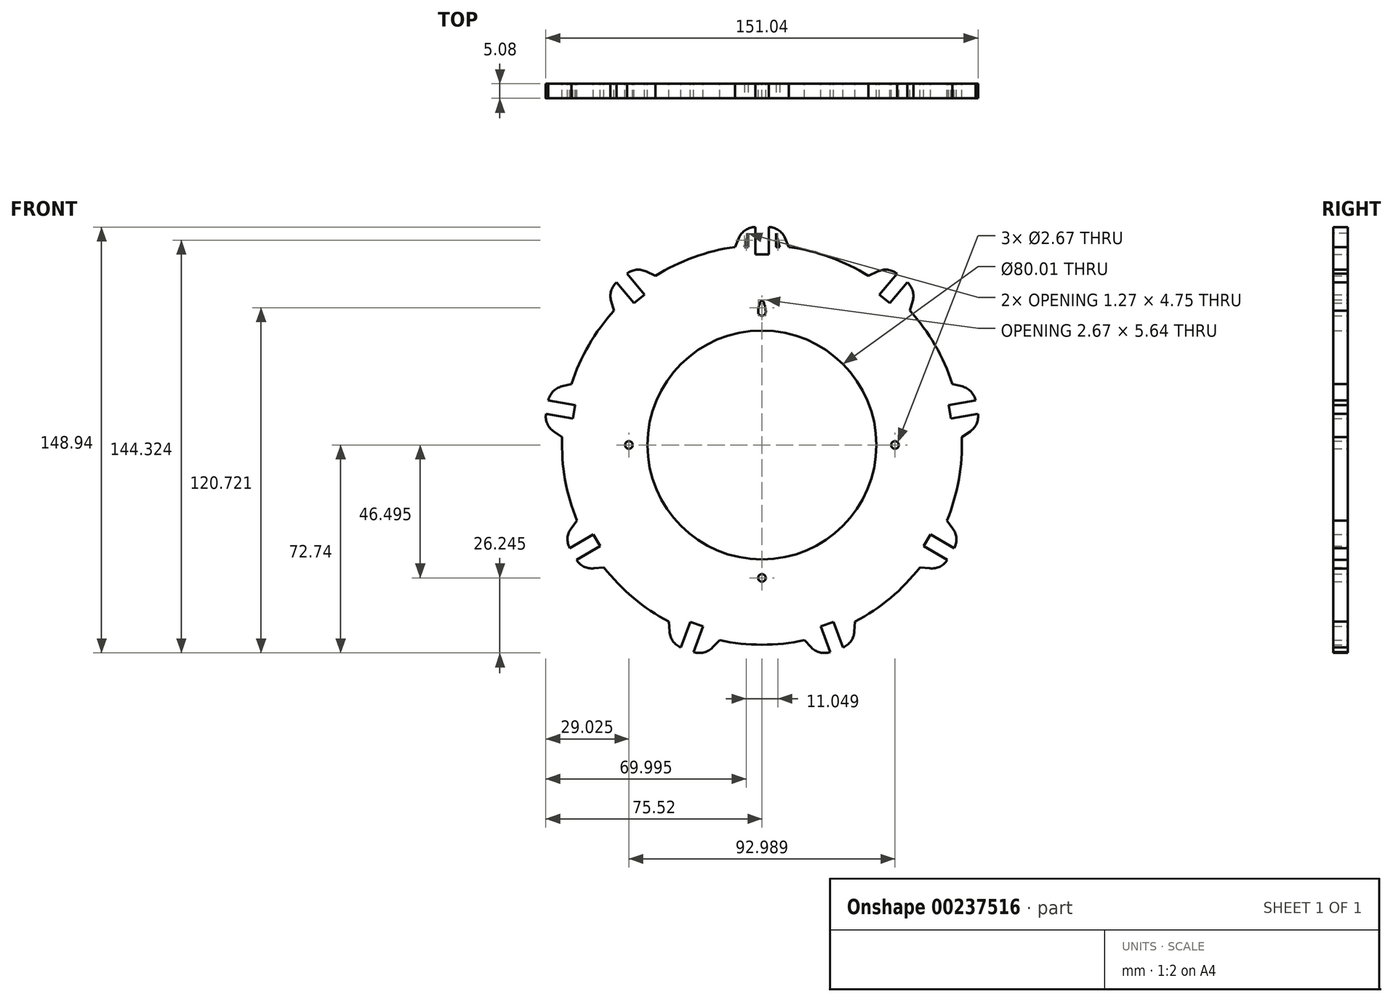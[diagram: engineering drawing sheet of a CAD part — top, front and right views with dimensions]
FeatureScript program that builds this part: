
annotation { "Feature Type Name" : "Feature", "Feature Type Description" : "" }
export const myFeature = defineFeature(function(context is Context, id is Id, definition is map)
    precondition{}
    {
        {
            var Q0;
            Q0=qCreatedBy(makeId("Front.planeOp"),FACE);
            var sketch = newSketch(context, id + "F0", { "sketchPlane" : qUnion([Q0])});
            skCircle(sketch, "E0", {"center": v(0, 0) * mm, "radius": 69.85 * mm});
            skCircle(sketch, "E1", {"center": v(0, 0) * mm, "radius": 40 * mm});
            skCircle(sketch, "E2", {"center": v(0, 0) * mm, "radius": 46.5 * mm, "construction": true});
            skPoint(sketch, "E3.center", {"position": v(0, -7.07) * mm});
            skLineSegment(sketch, "E4", {"start": v(-9.44, 69.2) * mm, "end": v(-8.02, 72.42) * mm});
            skLineSegment(sketch, "E5", {"start": v(-2.21, 76.2) * mm, "end": v(2.21, 76.2) * mm});
            skLineSegment(sketch, "E6", {"start": v(8.02, 72.42) * mm, "end": v(9.44, 69.2) * mm});
            skPoint(sketch, "E7", {"position": v(0, 76.2) * mm});
            skLineSegment(sketch, "E8", {"start": v(-9.44, 69.2) * mm, "end": v(-40, 0) * mm, "construction": true});
            skLineSegment(sketch, "E9", {"start": v(40, 0) * mm, "end": v(9.44, 69.2) * mm, "construction": true});
            skLineSegment(sketch, "E10", {"start": v(-2.35, 76.2) * mm, "end": v(-2.35, 66.67) * mm});
            skLineSegment(sketch, "E11", {"start": v(-2.35, 66.68) * mm, "end": v(2.35, 66.68) * mm});
            skLineSegment(sketch, "E12", {"start": v(2.35, 66.67) * mm, "end": v(2.35, 76.2) * mm});
            skPoint(sketch, "E13", {"position": v(0, 66.67) * mm});
            skPoint(sketch, "E14.visualSharp", {"position": v(-6.35, 76.2) * mm});
            skArc(sketch, "E14.filletArc", {"start": v(-2.21, 76.2) * mm, "mid": v(-5.68, 75.17) * mm, "end": v(-8.02, 72.42) * mm});
            skPoint(sketch, "E15.visualSharp", {"position": v(6.35, 76.2) * mm});
            skArc(sketch, "E15.filletArc", {"start": v(8.02, 72.42) * mm, "mid": v(5.68, 75.17) * mm, "end": v(2.21, 76.2) * mm});
            skCircle(sketch, "E16.MirrorC", {"center": v(0, 46.5) * mm, "radius": 1.33 * mm});
            skCircle(sketch, "E17", {"center": v(0, 0) * mm, "radius": 66.72 * mm, "construction": true});
            skCircle(sketch, "E18.1.0", {"center": v(-46.5, 0) * mm, "radius": 1.33 * mm});
            skCircle(sketch, "E18.2.0", {"center": v(0, -46.5) * mm, "radius": 1.33 * mm});
            skCircle(sketch, "E18.3.0", {"center": v(46.5, 0) * mm, "radius": 1.33 * mm});
            skCircle(sketch, "E19", {"center": v(0, 0) * mm, "radius": 50.8 * mm, "construction": true});
            skArc(sketch, "E20", {"start": v(1.33, 46.48) * mm, "mid": v(1, 48.74) * mm, "end": v(0, 50.8) * mm});
            skArc(sketch, "E21", {"start": v(0, 50.8) * mm, "mid": v(-1, 48.74) * mm, "end": v(-1.33, 46.48) * mm});
            skLineSegment(sketch, "E22.1.0", {"start": v(-51.72, 46.95) * mm, "end": v(-52.7, 50.32) * mm});
            skArc(sketch, "E22.1.1", {"start": v(-50.68, 56.95) * mm, "mid": v(-52.67, 53.93) * mm, "end": v(-52.7, 50.32) * mm});
            skLineSegment(sketch, "E22.1.2", {"start": v(-50.78, 56.86) * mm, "end": v(-44.66, 49.57) * mm});
            skLineSegment(sketch, "E22.1.3", {"start": v(-41.06, 52.59) * mm, "end": v(-47.18, 59.88) * mm});
            skArc(sketch, "E22.1.4", {"start": v(-40.4, 60.63) * mm, "mid": v(-43.97, 61.23) * mm, "end": v(-47.29, 59.8) * mm});
            skLineSegment(sketch, "E22.1.5", {"start": v(-40.4, 60.63) * mm, "end": v(-37.26, 59.08) * mm});
            skLineSegment(sketch, "E22.1.6", {"start": v(-44.66, 49.57) * mm, "end": v(-41.06, 52.59) * mm});
            skLineSegment(sketch, "E22.2.0", {"start": v(-69.8, 2.72) * mm, "end": v(-72.7, 4.68) * mm});
            skArc(sketch, "E22.2.1", {"start": v(-75.43, 11.05) * mm, "mid": v(-75.01, 7.46) * mm, "end": v(-72.7, 4.68) * mm});
            skLineSegment(sketch, "E22.2.2", {"start": v(-75.45, 10.92) * mm, "end": v(-66.07, 9.26) * mm});
            skLineSegment(sketch, "E22.2.3", {"start": v(-65.25, 13.9) * mm, "end": v(-74.63, 15.55) * mm});
            skArc(sketch, "E22.2.4", {"start": v(-69.92, 20.47) * mm, "mid": v(-73.04, 18.65) * mm, "end": v(-74.66, 15.41) * mm});
            skLineSegment(sketch, "E22.2.5", {"start": v(-69.92, 20.47) * mm, "end": v(-66.52, 21.31) * mm});
            skLineSegment(sketch, "E22.2.6", {"start": v(-66.07, 9.26) * mm, "end": v(-65.25, 13.9) * mm});
            skLineSegment(sketch, "E22.3.0", {"start": v(-55.22, -42.78) * mm, "end": v(-58.7, -43.15) * mm});
            skArc(sketch, "E22.3.1", {"start": v(-64.88, -40.02) * mm, "mid": v(-62.26, -42.5) * mm, "end": v(-58.7, -43.15) * mm});
            skLineSegment(sketch, "E22.3.2", {"start": v(-64.82, -40.13) * mm, "end": v(-56.57, -35.37) * mm});
            skLineSegment(sketch, "E22.3.3", {"start": v(-58.92, -31.3) * mm, "end": v(-67.17, -36.07) * mm});
            skArc(sketch, "E22.3.4", {"start": v(-66.72, -29.26) * mm, "mid": v(-67.94, -32.67) * mm, "end": v(-67.1, -36.18) * mm});
            skLineSegment(sketch, "E22.3.5", {"start": v(-66.72, -29.26) * mm, "end": v(-64.66, -26.43) * mm});
            skLineSegment(sketch, "E22.3.6", {"start": v(-56.57, -35.37) * mm, "end": v(-58.92, -31.3) * mm});
            skLineSegment(sketch, "E22.4.0", {"start": v(-14.8, -68.26) * mm, "end": v(-17.23, -70.8) * mm});
            skArc(sketch, "E22.4.1", {"start": v(-23.98, -72.36) * mm, "mid": v(-20.37, -72.58) * mm, "end": v(-17.23, -70.8) * mm});
            skLineSegment(sketch, "E22.4.2", {"start": v(-23.85, -72.4) * mm, "end": v(-20.6, -63.46) * mm});
            skLineSegment(sketch, "E22.4.3", {"start": v(-25.01, -61.85) * mm, "end": v(-28.27, -70.8) * mm});
            skArc(sketch, "E22.4.4", {"start": v(-32.3, -65.3) * mm, "mid": v(-31.05, -68.7) * mm, "end": v(-28.14, -70.85) * mm});
            skLineSegment(sketch, "E22.4.5", {"start": v(-32.3, -65.3) * mm, "end": v(-32.54, -61.8) * mm});
            skLineSegment(sketch, "E22.4.6", {"start": v(-20.6, -63.46) * mm, "end": v(-25.01, -61.85) * mm});
            skLineSegment(sketch, "E22.5.0", {"start": v(32.54, -61.8) * mm, "end": v(32.3, -65.3) * mm});
            skArc(sketch, "E22.5.1", {"start": v(28.14, -70.85) * mm, "mid": v(31.05, -68.7) * mm, "end": v(32.3, -65.3) * mm});
            skLineSegment(sketch, "E22.5.2", {"start": v(28.27, -70.8) * mm, "end": v(25.01, -61.85) * mm});
            skLineSegment(sketch, "E22.5.3", {"start": v(20.6, -63.46) * mm, "end": v(23.85, -72.4) * mm});
            skArc(sketch, "E22.5.4", {"start": v(17.23, -70.8) * mm, "mid": v(20.37, -72.58) * mm, "end": v(23.98, -72.36) * mm});
            skLineSegment(sketch, "E22.5.5", {"start": v(17.23, -70.8) * mm, "end": v(14.8, -68.26) * mm});
            skLineSegment(sketch, "E22.5.6", {"start": v(25.01, -61.85) * mm, "end": v(20.6, -63.46) * mm});
            skLineSegment(sketch, "E22.6.0", {"start": v(64.66, -26.43) * mm, "end": v(66.72, -29.26) * mm});
            skArc(sketch, "E22.6.1", {"start": v(67.1, -36.18) * mm, "mid": v(67.94, -32.67) * mm, "end": v(66.72, -29.26) * mm});
            skLineSegment(sketch, "E22.6.2", {"start": v(67.17, -36.07) * mm, "end": v(58.92, -31.3) * mm});
            skLineSegment(sketch, "E22.6.3", {"start": v(56.57, -35.37) * mm, "end": v(64.82, -40.13) * mm});
            skArc(sketch, "E22.6.4", {"start": v(58.7, -43.15) * mm, "mid": v(62.26, -42.5) * mm, "end": v(64.88, -40.02) * mm});
            skLineSegment(sketch, "E22.6.5", {"start": v(58.7, -43.15) * mm, "end": v(55.22, -42.78) * mm});
            skLineSegment(sketch, "E22.6.6", {"start": v(58.92, -31.3) * mm, "end": v(56.57, -35.37) * mm});
            skLineSegment(sketch, "E22.7.0", {"start": v(66.52, 21.31) * mm, "end": v(69.92, 20.47) * mm});
            skArc(sketch, "E22.7.1", {"start": v(74.66, 15.41) * mm, "mid": v(73.04, 18.65) * mm, "end": v(69.92, 20.47) * mm});
            skLineSegment(sketch, "E22.7.2", {"start": v(74.63, 15.55) * mm, "end": v(65.25, 13.9) * mm});
            skLineSegment(sketch, "E22.7.3", {"start": v(66.07, 9.26) * mm, "end": v(75.45, 10.92) * mm});
            skArc(sketch, "E22.7.4", {"start": v(72.7, 4.68) * mm, "mid": v(75.01, 7.46) * mm, "end": v(75.43, 11.05) * mm});
            skLineSegment(sketch, "E22.7.5", {"start": v(72.7, 4.68) * mm, "end": v(69.8, 2.72) * mm});
            skLineSegment(sketch, "E22.7.6", {"start": v(65.25, 13.9) * mm, "end": v(66.07, 9.26) * mm});
            skLineSegment(sketch, "E22.8.0", {"start": v(37.26, 59.08) * mm, "end": v(40.4, 60.63) * mm});
            skArc(sketch, "E22.8.1", {"start": v(47.29, 59.8) * mm, "mid": v(43.97, 61.23) * mm, "end": v(40.4, 60.63) * mm});
            skLineSegment(sketch, "E22.8.2", {"start": v(47.18, 59.88) * mm, "end": v(41.06, 52.59) * mm});
            skLineSegment(sketch, "E22.8.3", {"start": v(44.66, 49.57) * mm, "end": v(50.78, 56.86) * mm});
            skArc(sketch, "E22.8.4", {"start": v(52.7, 50.32) * mm, "mid": v(52.67, 53.93) * mm, "end": v(50.68, 56.95) * mm});
            skLineSegment(sketch, "E22.8.5", {"start": v(52.7, 50.32) * mm, "end": v(51.72, 46.95) * mm});
            skLineSegment(sketch, "E22.8.6", {"start": v(41.06, 52.59) * mm, "end": v(44.66, 49.57) * mm});
            skSolve(sketch);
        }
        {
            var Q0;
            Q0=makeQuery(id+"F0.imprint","IMPRINT",FACE,{"disambiguationData":[TD([[makeQuery(id+"F0.imprint","IMPRINT",EDGE,{"derivedFrom":sQuery(id+"F0.wireOp",EDGE,"E1")}),-1.0]])]});
            var Q1;
            {var subQ0=sQuery(id+"F0.wireOp",EDGE,"E22.1.5");Q1=makeQuery(id+"F0.imprint","IMPRINT",FACE,{"disambiguationData":[TD([[makeQuery(id+"F0.imprint","IMPRINT",EDGE,{"derivedFrom":subQ0}),-1.0]])]});}
            var Q2;
            {var subQ0=sQuery(id+"F0.wireOp",EDGE,"E22.1.0");Q2=makeQuery(id+"F0.imprint","IMPRINT",FACE,{"disambiguationData":[TD([[makeQuery(id+"F0.imprint","IMPRINT",EDGE,{"derivedFrom":subQ0}),-1.0]])]});}
            var Q3;
            {var subQ0=sQuery(id+"F0.wireOp",EDGE,"E4");Q3=makeQuery(id+"F0.imprint","IMPRINT",FACE,{"disambiguationData":[TD([[makeQuery(id+"F0.imprint","IMPRINT",EDGE,{"derivedFrom":subQ0}),-1.0]])]});}
            var Q4;
            {var subQ0=sQuery(id+"F0.wireOp",EDGE,"E6");Q4=makeQuery(id+"F0.imprint","IMPRINT",FACE,{"disambiguationData":[TD([[makeQuery(id+"F0.imprint","IMPRINT",EDGE,{"derivedFrom":subQ0}),-1.0]])]});}
            var Q5;
            {var subQ0=sQuery(id+"F0.wireOp",EDGE,"E22.8.0");Q5=makeQuery(id+"F0.imprint","IMPRINT",FACE,{"disambiguationData":[TD([[makeQuery(id+"F0.imprint","IMPRINT",EDGE,{"derivedFrom":subQ0}),-1.0]])]});}
            var Q6;
            {var subQ0=sQuery(id+"F0.wireOp",EDGE,"E22.8.5");Q6=makeQuery(id+"F0.imprint","IMPRINT",FACE,{"disambiguationData":[TD([[makeQuery(id+"F0.imprint","IMPRINT",EDGE,{"derivedFrom":subQ0}),-1.0]])]});}
            var Q7;
            {var subQ0=sQuery(id+"F0.wireOp",EDGE,"E22.7.0");Q7=makeQuery(id+"F0.imprint","IMPRINT",FACE,{"disambiguationData":[TD([[makeQuery(id+"F0.imprint","IMPRINT",EDGE,{"derivedFrom":subQ0}),-1.0]])]});}
            var Q8;
            {var subQ0=sQuery(id+"F0.wireOp",EDGE,"E22.7.5");Q8=makeQuery(id+"F0.imprint","IMPRINT",FACE,{"disambiguationData":[TD([[makeQuery(id+"F0.imprint","IMPRINT",EDGE,{"derivedFrom":subQ0}),-1.0]])]});}
            var Q9;
            {var subQ0=sQuery(id+"F0.wireOp",EDGE,"E22.6.0");Q9=makeQuery(id+"F0.imprint","IMPRINT",FACE,{"disambiguationData":[TD([[makeQuery(id+"F0.imprint","IMPRINT",EDGE,{"derivedFrom":subQ0}),-1.0]])]});}
            var Q10;
            {var subQ0=sQuery(id+"F0.wireOp",EDGE,"E22.6.5");Q10=makeQuery(id+"F0.imprint","IMPRINT",FACE,{"disambiguationData":[TD([[makeQuery(id+"F0.imprint","IMPRINT",EDGE,{"derivedFrom":subQ0}),-1.0]])]});}
            var Q11;
            {var subQ0=sQuery(id+"F0.wireOp",EDGE,"E22.5.5");Q11=makeQuery(id+"F0.imprint","IMPRINT",FACE,{"disambiguationData":[TD([[makeQuery(id+"F0.imprint","IMPRINT",EDGE,{"derivedFrom":subQ0}),-1.0]])]});}
            var Q12;
            {var subQ0=sQuery(id+"F0.wireOp",EDGE,"E22.5.0");Q12=makeQuery(id+"F0.imprint","IMPRINT",FACE,{"disambiguationData":[TD([[makeQuery(id+"F0.imprint","IMPRINT",EDGE,{"derivedFrom":subQ0}),-1.0]])]});}
            var Q13;
            {var subQ0=sQuery(id+"F0.wireOp",EDGE,"E22.4.5");Q13=makeQuery(id+"F0.imprint","IMPRINT",FACE,{"disambiguationData":[TD([[makeQuery(id+"F0.imprint","IMPRINT",EDGE,{"derivedFrom":subQ0}),-1.0]])]});}
            var Q14;
            {var subQ0=sQuery(id+"F0.wireOp",EDGE,"E22.4.0");Q14=makeQuery(id+"F0.imprint","IMPRINT",FACE,{"disambiguationData":[TD([[makeQuery(id+"F0.imprint","IMPRINT",EDGE,{"derivedFrom":subQ0}),-1.0]])]});}
            var Q15;
            {var subQ0=sQuery(id+"F0.wireOp",EDGE,"E22.3.0");Q15=makeQuery(id+"F0.imprint","IMPRINT",FACE,{"disambiguationData":[TD([[makeQuery(id+"F0.imprint","IMPRINT",EDGE,{"derivedFrom":subQ0}),-1.0]])]});}
            var Q16;
            {var subQ0=sQuery(id+"F0.wireOp",EDGE,"E22.3.5");Q16=makeQuery(id+"F0.imprint","IMPRINT",FACE,{"disambiguationData":[TD([[makeQuery(id+"F0.imprint","IMPRINT",EDGE,{"derivedFrom":subQ0}),-1.0]])]});}
            var Q17;
            {var subQ0=sQuery(id+"F0.wireOp",EDGE,"E22.2.0");Q17=makeQuery(id+"F0.imprint","IMPRINT",FACE,{"disambiguationData":[TD([[makeQuery(id+"F0.imprint","IMPRINT",EDGE,{"derivedFrom":subQ0}),-1.0]])]});}
            var Q18;
            {var subQ0=sQuery(id+"F0.wireOp",EDGE,"E22.2.5");Q18=makeQuery(id+"F0.imprint","IMPRINT",FACE,{"disambiguationData":[TD([[makeQuery(id+"F0.imprint","IMPRINT",EDGE,{"derivedFrom":subQ0}),-1.0]])]});}
            extrude(context, id + "F1", {"entities" : qUnion([Q0, Q1, Q2, Q3, Q4, Q5, Q6, Q7, Q8, Q9, Q10, Q11, Q12, Q13, Q14, Q15, Q16, Q17, Q18]), "depth" : 5.08 * mm});
        }
        {
            var Q0;
            {var subQ0=sQuery(id+"FvJpxpYg898pNAX_1.wireOp",EDGE,"53E3jjuS-hRJ3-EJHB-q42a-zf0OxQkTzMQm");var subQ1=sQuery(id+"FvJpxpYg898pNAX_1.wireOp",EDGE,"eDTWx6nS-4LiB-bQoC-8h4n-UFIUxgX0mG1X");var subQ2=sQuery(id+"FvJpxpYg898pNAX_1.wireOp",EDGE,"w75uQd79-OuTk-zNXF-Czll-kn5tBHbynTvD");var subQ3=sQuery(id+"FvJpxpYg898pNAX_1.wireOp",EDGE,"Ia1vBbiV-KCZw-VCwM-2Djj-mJQj9exYNCmG");var subQ4=sQuery(id+"F0.wireOp",EDGE,"E22.4.5");var subQ5=sQuery(id+"F0.wireOp",EDGE,"E22.3.6");var subQ6=sQuery(id+"F0.wireOp",EDGE,"E22.3.4");var subQ7=sQuery(id+"F0.wireOp",EDGE,"E22.4.2");var subQ8=sQuery(id+"F0.wireOp",EDGE,"E22.3.2");var subQ9=sQuery(id+"F0.wireOp",EDGE,"E22.4.4");var subQ10=sQuery(id+"F0.wireOp",EDGE,"E22.3.3");var subQ11=sQuery(id+"F0.wireOp",EDGE,"E22.3.1");var subQ12=sQuery(id+"F0.wireOp",EDGE,"E22.4.0");var subQ13=sQuery(id+"F0.wireOp",EDGE,"E22.2.6");var subQ14=sQuery(id+"F0.wireOp",EDGE,"E22.2.4");var subQ15=sQuery(id+"F0.wireOp",EDGE,"E22.2.2");var subQ16=sQuery(id+"F0.wireOp",EDGE,"E22.2.0");var subQ17=sQuery(id+"F0.wireOp",EDGE,"E22.1.2");var subQ18=sQuery(id+"F0.wireOp",EDGE,"E22.1.6");var subQ19=sQuery(id+"F0.wireOp",EDGE,"E22.5.0");var subQ20=sQuery(id+"F0.wireOp",EDGE,"E0");var subQ21=sQuery(id+"F0.wireOp",EDGE,"E22.6.5");var subQ22=sQuery(id+"F0.wireOp",EDGE,"E22.6.1");var subQ23=sQuery(id+"F0.wireOp",EDGE,"E12");var subQ24=sQuery(id+"F0.wireOp",EDGE,"E22.5.5");var subQ25=sQuery(id+"F0.wireOp",EDGE,"E22.3.0");var subQ26=sQuery(id+"F0.wireOp",EDGE,"E22.7.5");var subQ27=sQuery(id+"F0.wireOp",EDGE,"E22.3.5");var subQ28=sQuery(id+"F0.wireOp",EDGE,"E22.4.3");var subQ29=sQuery(id+"F0.wireOp",EDGE,"E22.8.5");var subQ30=sQuery(id+"F0.wireOp",EDGE,"E22.7.0");var subQ31=sQuery(id+"F0.wireOp",EDGE,"E22.1.1");var subQ32=sQuery(id+"F0.wireOp",EDGE,"E22.8.4");var subQ33=sQuery(id+"F0.wireOp",EDGE,"E14.filletArc");var subQ34=sQuery(id+"F0.wireOp",EDGE,"E22.6.0");var subQ35=sQuery(id+"F0.wireOp",EDGE,"E22.1.3");var subQ36=sQuery(id+"F0.wireOp",EDGE,"E22.8.6");var subQ37=sQuery(id+"F0.wireOp",EDGE,"E6");var subQ38=sQuery(id+"F0.wireOp",EDGE,"E22.8.0");var subQ39=sQuery(id+"F0.wireOp",EDGE,"E22.7.1");var subQ40=sQuery(id+"F0.wireOp",EDGE,"E4");var subQ41=sQuery(id+"F0.wireOp",EDGE,"E22.1.5");var subQ42=sQuery(id+"F0.wireOp",EDGE,"E22.6.4");var subQ43=sQuery(id+"F0.wireOp",EDGE,"E22.5.1");var subQ44=sQuery(id+"F0.wireOp",EDGE,"E22.4.6");var subQ45=sQuery(id+"F0.wireOp",EDGE,"E22.1.0");var subQ46=sQuery(id+"F0.wireOp",EDGE,"E22.2.5");var subQ47=sQuery(id+"F0.wireOp",EDGE,"E10");var subQ48=sQuery(id+"F0.wireOp",EDGE,"E22.6.6");var subQ49=sQuery(id+"F0.wireOp",EDGE,"E11");var subQ50=sQuery(id+"F0.wireOp",EDGE,"E15.filletArc");var subQ51=sQuery(id+"F0.wireOp",EDGE,"E22.2.3");var subQ52=sQuery(id+"F0.wireOp",EDGE,"E22.2.1");var subQ53=sQuery(id+"F0.wireOp",EDGE,"E22.4.1");var subQ54=sQuery(id+"F0.wireOp",EDGE,"E22.1.4");var subQ55=sQuery(id+"F0.wireOp",EDGE,"E22.5.2");var subQ56=sQuery(id+"F0.wireOp",EDGE,"E22.8.3");var subQ57=sQuery(id+"F0.wireOp",EDGE,"E22.5.3");var subQ58=sQuery(id+"F0.wireOp",EDGE,"E22.5.4");var subQ59=sQuery(id+"F0.wireOp",EDGE,"E22.5.6");var subQ60=sQuery(id+"F0.wireOp",EDGE,"E22.6.2");var subQ61=sQuery(id+"F0.wireOp",EDGE,"E22.6.3");var subQ62=sQuery(id+"F0.wireOp",EDGE,"E22.7.2");var subQ63=sQuery(id+"F0.wireOp",EDGE,"E22.7.3");var subQ64=sQuery(id+"F0.wireOp",EDGE,"E22.7.4");var subQ65=sQuery(id+"F0.wireOp",EDGE,"E22.7.6");var subQ66=sQuery(id+"F0.wireOp",EDGE,"E22.8.1");var subQ67=sQuery(id+"F0.wireOp",EDGE,"E22.8.2");Q0=makeQuery(id+"Fi6H0UMDYzaO5z0_1.1.FCaG3GybYMWkdXD_1.boolean.opBoolean","MERGE",FACE,{"derivedFrom":[makeQuery(id+"FCaG3GybYMWkdXD_1.boolean.opBoolean","MERGE",FACE,{"derivedFrom":[makeQuery(id+"FytycAvAVJUMnGM_1.boolean.opBoolean","SPLIT",FACE,{"disambiguationData":[TD([makeQuery(id+"F1.opExtrude","SWEPT_FACE",FACE,{"disambiguationData":[OSD([subQ40])]})])],"derivedFrom":makeQuery(id+"F1.opExtrude","CAP_FACE",FACE,{"disambiguationData":[OSD([subQ20,sQuery(id+"F0.wireOp",EDGE,"E1"),subQ40,subQ37,subQ47,subQ49,subQ23,subQ33,subQ50,sQuery(id+"F0.wireOp",EDGE,"E16.MirrorC"),sQuery(id+"F0.wireOp",EDGE,"E18.1.0"),sQuery(id+"F0.wireOp",EDGE,"E18.2.0"),sQuery(id+"F0.wireOp",EDGE,"E18.3.0"),sQuery(id+"F0.wireOp",EDGE,"E20"),sQuery(id+"F0.wireOp",EDGE,"E21"),subQ45,subQ31,subQ17,subQ35,subQ54,subQ41,subQ18,subQ16,subQ52,subQ15,subQ51,subQ14,subQ46,subQ13,subQ25,subQ11,subQ8,subQ10,subQ6,subQ27,subQ5,subQ12,subQ53,subQ7,subQ28,subQ9,subQ4,subQ44,subQ19,subQ43,subQ55,subQ57,subQ58,subQ24,subQ59,subQ34,subQ22,subQ60,subQ61,subQ42,subQ21,subQ48,subQ30,subQ39,subQ62,subQ63,subQ64,subQ26,subQ65,subQ38,subQ66,subQ67,subQ56,subQ32,subQ29,subQ36])],"isStart":false})}),makeQuery(id+"FCaG3GybYMWkdXD_1.opExtrude","CAP_FACE",FACE,{"disambiguationData":[OSD([subQ3,subQ2,subQ1,subQ0])],"isStart":true})]}),makeQuery(id+"Fi6H0UMDYzaO5z0_1.1.FCaG3GybYMWkdXD_1.opExtrude","CAP_FACE",FACE,{"disambiguationData":[OSD([subQ3,subQ2,subQ1,subQ0])],"isStart":true})]});}
            var sketch = newSketch(context, id + "F2", { "sketchPlane" : qUnion([Q0])});
            skLineSegment(sketch, "E23", {"start": v(-4.89, 73.96) * mm, "end": v(-4.89, 69.2) * mm});
            skLineSegment(sketch, "E24", {"start": v(4.89, 73.96) * mm, "end": v(4.89, 69.2) * mm});
            skLineSegment(sketch, "E25", {"start": v(4.89, 69.2) * mm, "end": v(6.16, 69.2) * mm});
            skLineSegment(sketch, "E26", {"start": v(-4.89, 69.2) * mm, "end": v(-6.16, 69.2) * mm});
            skLineSegment(sketch, "E27", {"start": v(-4.89, 73.96) * mm, "end": v(-6.16, 69.2) * mm});
            skLineSegment(sketch, "E28", {"start": v(4.89, 73.96) * mm, "end": v(6.16, 69.2) * mm});
            skLineSegment(sketch, "E29", {"start": v(-6.35, 76.2) * mm, "end": v(-4.89, 73.96) * mm, "construction": true});
            skLineSegment(sketch, "E30", {"start": v(6.35, 76.2) * mm, "end": v(4.89, 73.96) * mm, "construction": true});
            skSolve(sketch);
        }
        {
            var Q0;
            Q0=makeQuery(id+"F2.imprint","IMPRINT",FACE,{"disambiguationData":[TD([[makeQuery(id+"F2.imprint","IMPRINT",EDGE,{"derivedFrom":sQuery(id+"F2.wireOp",EDGE,"E23")}),-1.0]])]});
            var Q1;
            Q1=makeQuery(id+"F2.imprint","IMPRINT",FACE,{"disambiguationData":[TD([[makeQuery(id+"F2.imprint","IMPRINT",EDGE,{"derivedFrom":sQuery(id+"F2.wireOp",EDGE,"E24")}),1.0]])]});
            var Q2;
            Q2=makeQuery(id+"F1.opExtrude","CAP_FACE",FACE,{"disambiguationData":[OSD([sQuery(id+"F0.wireOp",EDGE,"E0"),sQuery(id+"F0.wireOp",EDGE,"E1"),sQuery(id+"F0.wireOp",EDGE,"E4"),sQuery(id+"F0.wireOp",EDGE,"E6"),sQuery(id+"F0.wireOp",EDGE,"E10"),sQuery(id+"F0.wireOp",EDGE,"E11"),sQuery(id+"F0.wireOp",EDGE,"E12"),sQuery(id+"F0.wireOp",EDGE,"E14.filletArc"),sQuery(id+"F0.wireOp",EDGE,"E15.filletArc"),sQuery(id+"F0.wireOp",EDGE,"E16.MirrorC"),sQuery(id+"F0.wireOp",EDGE,"E18.1.0"),sQuery(id+"F0.wireOp",EDGE,"E18.2.0"),sQuery(id+"F0.wireOp",EDGE,"E18.3.0"),sQuery(id+"F0.wireOp",EDGE,"E20"),sQuery(id+"F0.wireOp",EDGE,"E21"),sQuery(id+"F0.wireOp",EDGE,"E22.1.0"),sQuery(id+"F0.wireOp",EDGE,"E22.1.1"),sQuery(id+"F0.wireOp",EDGE,"E22.1.2"),sQuery(id+"F0.wireOp",EDGE,"E22.1.3"),sQuery(id+"F0.wireOp",EDGE,"E22.1.4"),sQuery(id+"F0.wireOp",EDGE,"E22.1.5"),sQuery(id+"F0.wireOp",EDGE,"E22.1.6"),sQuery(id+"F0.wireOp",EDGE,"E22.2.0"),sQuery(id+"F0.wireOp",EDGE,"E22.2.1"),sQuery(id+"F0.wireOp",EDGE,"E22.2.2"),sQuery(id+"F0.wireOp",EDGE,"E22.2.3"),sQuery(id+"F0.wireOp",EDGE,"E22.2.4"),sQuery(id+"F0.wireOp",EDGE,"E22.2.5"),sQuery(id+"F0.wireOp",EDGE,"E22.2.6"),sQuery(id+"F0.wireOp",EDGE,"E22.3.0"),sQuery(id+"F0.wireOp",EDGE,"E22.3.1"),sQuery(id+"F0.wireOp",EDGE,"E22.3.2"),sQuery(id+"F0.wireOp",EDGE,"E22.3.3"),sQuery(id+"F0.wireOp",EDGE,"E22.3.4"),sQuery(id+"F0.wireOp",EDGE,"E22.3.5"),sQuery(id+"F0.wireOp",EDGE,"E22.3.6"),sQuery(id+"F0.wireOp",EDGE,"E22.4.0"),sQuery(id+"F0.wireOp",EDGE,"E22.4.1"),sQuery(id+"F0.wireOp",EDGE,"E22.4.2"),sQuery(id+"F0.wireOp",EDGE,"E22.4.3"),sQuery(id+"F0.wireOp",EDGE,"E22.4.4"),sQuery(id+"F0.wireOp",EDGE,"E22.4.5"),sQuery(id+"F0.wireOp",EDGE,"E22.4.6"),sQuery(id+"F0.wireOp",EDGE,"E22.5.0"),sQuery(id+"F0.wireOp",EDGE,"E22.5.1"),sQuery(id+"F0.wireOp",EDGE,"E22.5.2"),sQuery(id+"F0.wireOp",EDGE,"E22.5.3"),sQuery(id+"F0.wireOp",EDGE,"E22.5.4"),sQuery(id+"F0.wireOp",EDGE,"E22.5.5"),sQuery(id+"F0.wireOp",EDGE,"E22.5.6"),sQuery(id+"F0.wireOp",EDGE,"E22.6.0"),sQuery(id+"F0.wireOp",EDGE,"E22.6.1"),sQuery(id+"F0.wireOp",EDGE,"E22.6.2"),sQuery(id+"F0.wireOp",EDGE,"E22.6.3"),sQuery(id+"F0.wireOp",EDGE,"E22.6.4"),sQuery(id+"F0.wireOp",EDGE,"E22.6.5"),sQuery(id+"F0.wireOp",EDGE,"E22.6.6"),sQuery(id+"F0.wireOp",EDGE,"E22.7.0"),sQuery(id+"F0.wireOp",EDGE,"E22.7.1"),sQuery(id+"F0.wireOp",EDGE,"E22.7.2"),sQuery(id+"F0.wireOp",EDGE,"E22.7.3"),sQuery(id+"F0.wireOp",EDGE,"E22.7.4"),sQuery(id+"F0.wireOp",EDGE,"E22.7.5"),sQuery(id+"F0.wireOp",EDGE,"E22.7.6"),sQuery(id+"F0.wireOp",EDGE,"E22.8.0"),sQuery(id+"F0.wireOp",EDGE,"E22.8.1"),sQuery(id+"F0.wireOp",EDGE,"E22.8.2"),sQuery(id+"F0.wireOp",EDGE,"E22.8.3"),sQuery(id+"F0.wireOp",EDGE,"E22.8.4"),sQuery(id+"F0.wireOp",EDGE,"E22.8.5"),sQuery(id+"F0.wireOp",EDGE,"E22.8.6")])],"isStart":true});
            extrude(context, id + "F3", {"entities" : qUnion([Q0, Q1]), "operationType" : NewBodyOperationType.REMOVE, "endBound" : BoundingType.UP_TO_SURFACE, "oppositeDirection" : true, "endBoundEntityFace" : qUnion([Q2]), "depth" : 25.4 * mm});
        }
    });
